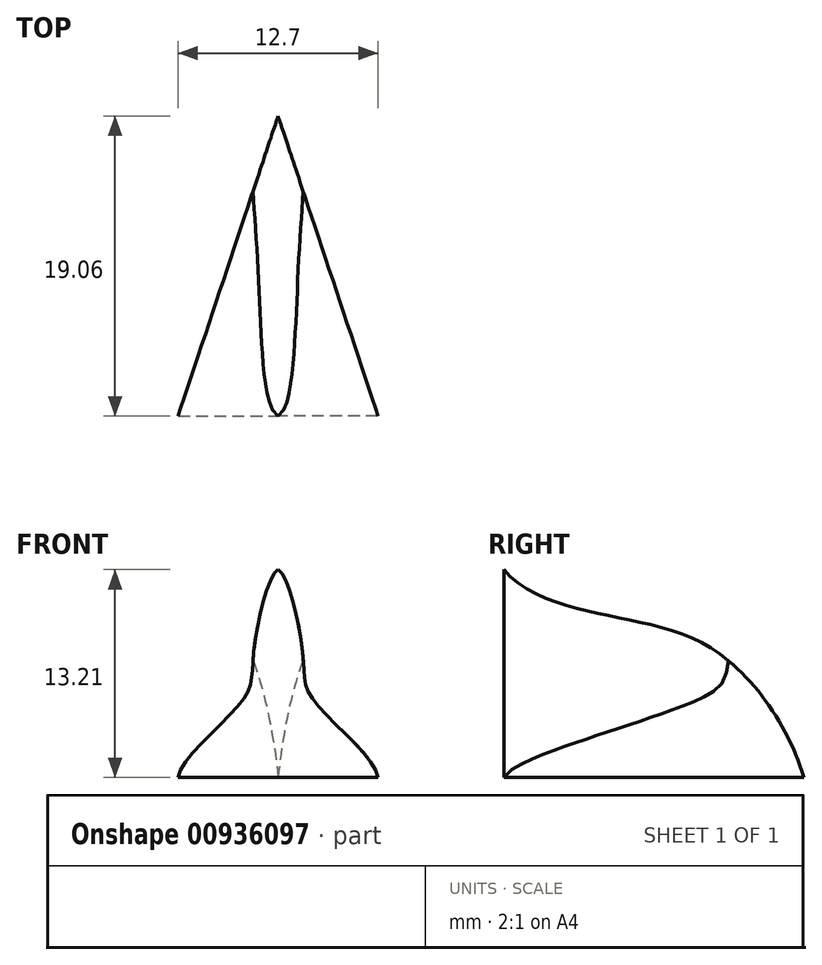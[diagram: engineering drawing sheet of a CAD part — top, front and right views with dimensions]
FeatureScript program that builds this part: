
annotation { "Feature Type Name" : "Feature", "Feature Type Description" : "" }
export const myFeature = defineFeature(function(context is Context, id is Id, definition is map)
    precondition{}
    {
        {
            var Q0;
            Q0=qCreatedBy(makeId("Top.planeOp"),FACE);
            var sketch = newSketch(context, id + "F0", { "sketchPlane" : qUnion([Q0])});
            skLineSegment(sketch, "E0.bottom", {"start": v(6.35, 9.53) * mm, "end": v(-6.35, 9.53) * mm});
            skLineSegment(sketch, "E0.top", {"start": v(6.35, -9.53) * mm, "end": v(-6.35, -9.53) * mm});
            skLineSegment(sketch, "E0.left", {"start": v(6.35, 9.53) * mm, "end": v(6.35, -9.53) * mm});
            skLineSegment(sketch, "E0.right", {"start": v(-6.35, 9.53) * mm, "end": v(-6.35, -9.53) * mm});
            skPoint(sketch, "E0.middle", {"position": v(0, 0) * mm});
            skSolve(sketch);
        }
        {
            var Q0;
            Q0=qCreatedBy(makeId("Front.planeOp"),FACE);
            var sketch = newSketch(context, id + "F1", { "sketchPlane" : qUnion([Q0])});
            skFitSpline(sketch, "E1", {"points": [v(-6.35, 0) * mm, v(-2.25, 4.93) * mm, v(-1.56, 7.85) * mm, v(0, 13.21) * mm], "startDerivative": vector(1.1, 10.13) * mm, "endDerivative": vector(5.64, 3.12) * mm});
            skFitSpline(sketch, "E2.MirrorCS", {"points": [v(6.35, 0) * mm, v(2.25, 4.93) * mm, v(1.56, 7.85) * mm, v(0, 13.21) * mm], "startDerivative": vector(-1.1, 10.13) * mm, "endDerivative": vector(-5.64, 3.12) * mm});
            skLineSegment(sketch, "E3.0", {"start": v(6.35, 0) * mm, "end": v(-6.35, 0) * mm});
            skSolve(sketch);
        }
        {
            var Q0;
            Q0 = qSketchRegion(id + "F1", true);
            extrude(context, id + "F2", {"entities" : qUnion([Q0]), "depth" : 9.52 * mm, "offsetDistance" : 25.4 * mm, "hasSecondDirection" : true, "secondDirectionOppositeDirection" : true, "secondDirectionDepth" : 9.52 * mm});
        }
        {
            var Q0;
            Q0=qCreatedBy(makeId("Right.planeOp"),FACE);
            var sketch = newSketch(context, id + "F3", { "sketchPlane" : qUnion([Q0])});
            skFitSpline(sketch, "E4", {"points": [v(9.53, 0) * mm, v(5.21, 7) * mm, v(0, 9.66) * mm, v(-9.53, 13.21) * mm], "startDerivative": vector(-8.14, 26.77) * mm, "endDerivative": vector(-14.17, 18.63) * mm});
            skFitSpline(sketch, "E5.0.1", {"points": [v(9.53, 0) * mm, v(9.53, 1.3) * mm, v(9.53, 5.02) * mm, v(9.53, 7.34) * mm, v(9.53, 12.84) * mm, v(9.53, 13.21) * mm]});
            skFitSpline(sketch, "E5.0.2", {"points": [v(9.53, 13.21) * mm, v(9.53, 12.84) * mm, v(9.53, 7.34) * mm, v(9.53, 5.02) * mm, v(9.53, 1.3) * mm, v(9.53, 0) * mm]});
            skLineSegment(sketch, "E5.1", {"start": v(-9.53, 13.21) * mm, "end": v(9.52, 13.21) * mm});
            skSolve(sketch);
        }
        {
            var Q0;
            Q0 = qSketchRegion(id + "F3", true);
            extrude(context, id + "F4", {"entities" : qUnion([Q0]), "operationType" : NewBodyOperationType.REMOVE, "depth" : 25.4 * mm, "offsetDistance" : 25.4 * mm, "hasSecondDirection" : true, "secondDirectionOppositeDirection" : true, "secondDirectionDepth" : 25.4 * mm});
        }
        {
            var Q0;
            Q0=qCreatedBy(makeId("Top.planeOp"),FACE);
            var sketch = newSketch(context, id + "F5", { "sketchPlane" : qUnion([Q0])});
            skLineSegment(sketch, "E6", {"start": v(-6.35, -9.53) * mm, "end": v(0, 9.53) * mm});
            skLineSegment(sketch, "E7.MirrorCS", {"start": v(6.35, -9.53) * mm, "end": v(0, 9.53) * mm});
            skLineSegment(sketch, "E8", {"start": v(-6.35, -9.53) * mm, "end": v(6.35, -9.53) * mm});
            skSolve(sketch);
        }
        {
            var Q0;
            Q0 = qSketchRegion(id + "F5", true);
            extrude(context, id + "F6", {"entities" : qUnion([Q0]), "operationType" : NewBodyOperationType.INTERSECT, "depth" : 25.4 * mm, "offsetDistance" : 25.4 * mm});
        }
    });
